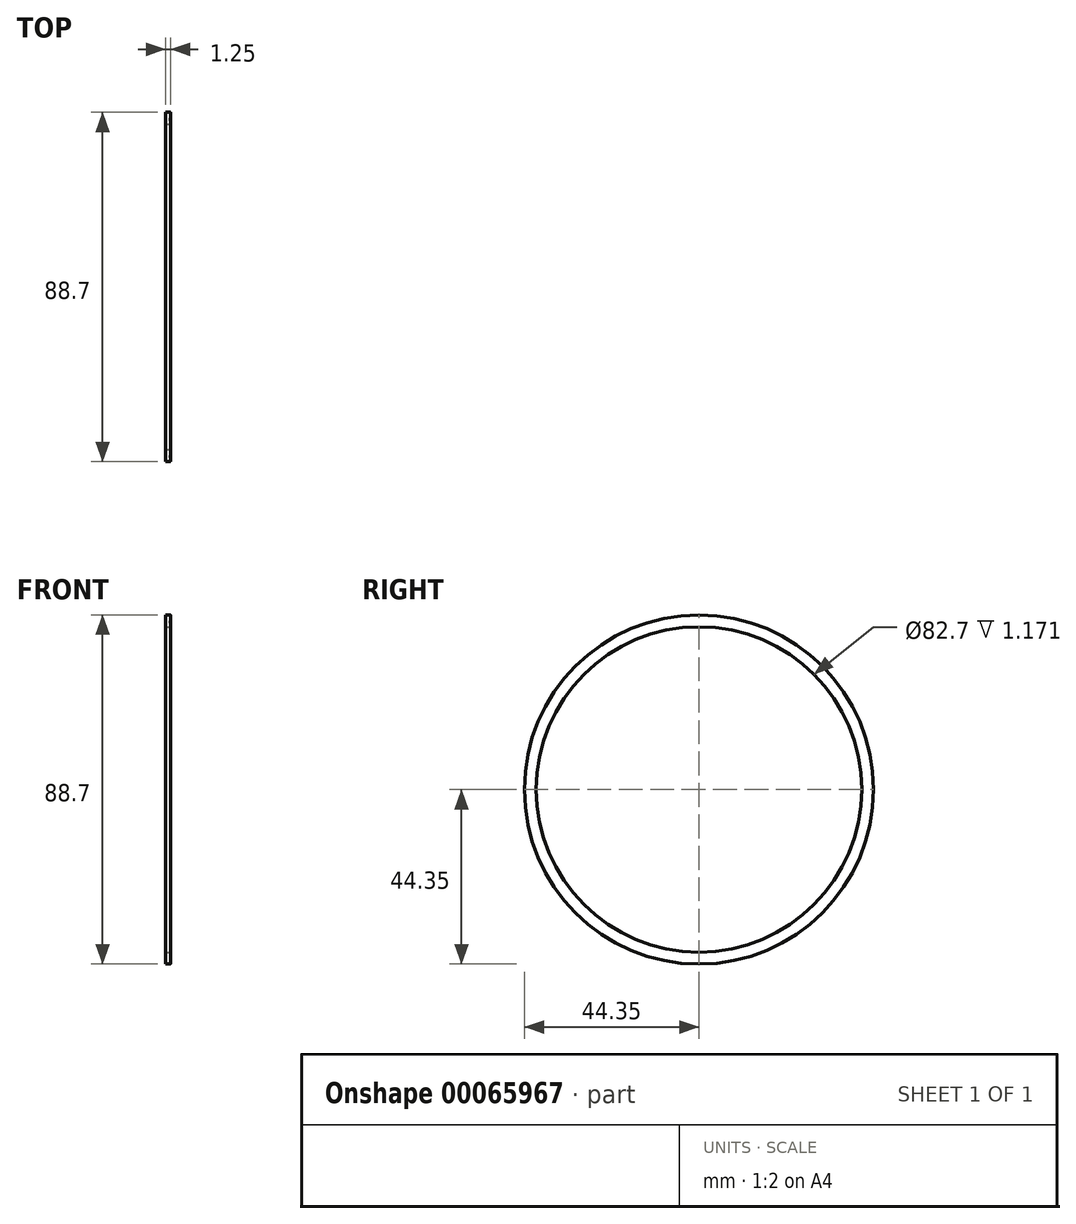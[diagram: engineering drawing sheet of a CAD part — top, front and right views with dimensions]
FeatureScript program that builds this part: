
annotation { "Feature Type Name" : "Feature", "Feature Type Description" : "" }
export const myFeature = defineFeature(function(context is Context, id is Id, definition is map)
    precondition{}
    {
        {
            var Q0;
            Q0=qCreatedBy(makeId("Front.planeOp"),FACE);
            var sketch = newSketch(context, id + "F0", { "sketchPlane" : qUnion([Q0])});
            skLineSegment(sketch, "E0.bottom", {"start": v(-0.1, 44.35) * mm, "end": v(-1.28, 44.35) * mm});
            skLineSegment(sketch, "E0.top", {"start": v(-0.1, 41.35) * mm, "end": v(-1.28, 41.35) * mm});
            skLineSegment(sketch, "E0.right", {"start": v(-1.28, 44.35) * mm, "end": v(-1.28, 41.35) * mm});
            skLineSegment(sketch, "E1", {"start": v(0, 0) * mm, "end": v(-6.16, 0) * mm, "construction": true});
            skArc(sketch, "E2", {"start": v(-0.03, 44.25) * mm, "mid": v(-0.26, 42.85) * mm, "end": v(-0.03, 41.45) * mm});
            skPoint(sketch, "E3.visualSharp", {"position": v(0, 44.35) * mm});
            skArc(sketch, "E3.filletArc", {"start": v(-0.03, 44.25) * mm, "mid": v(-0.05, 44.32) * mm, "end": v(-0.1, 44.35) * mm});
            skPoint(sketch, "E4.visualSharp", {"position": v(0, 41.35) * mm});
            skArc(sketch, "E4.filletArc", {"start": v(-0.1, 41.35) * mm, "mid": v(-0.05, 41.38) * mm, "end": v(-0.03, 41.45) * mm});
            skLineSegment(sketch, "E5", {"start": v(0, 41.35) * mm, "end": v(0, 0) * mm, "construction": true});
            skSolve(sketch);
        }
        {
            var Q0;
            Q0=makeQuery(id+"F0.imprint","IMPRINT",FACE,{"disambiguationData":[TD([[makeQuery(id+"F0.imprint","IMPRINT",EDGE,{"derivedFrom":sQuery(id+"F0.wireOp",EDGE,"E0.bottom")}),1.0]])]});
            var Q1;
            Q1=sQuery(id+"F0.wireOp",EDGE,"E1");
            revolve(context, id + "F1", {"entities" : qUnion([Q0]), "axis" : qUnion([Q1]), "revolveType" : RevolveType.FULL});
        }
    });
